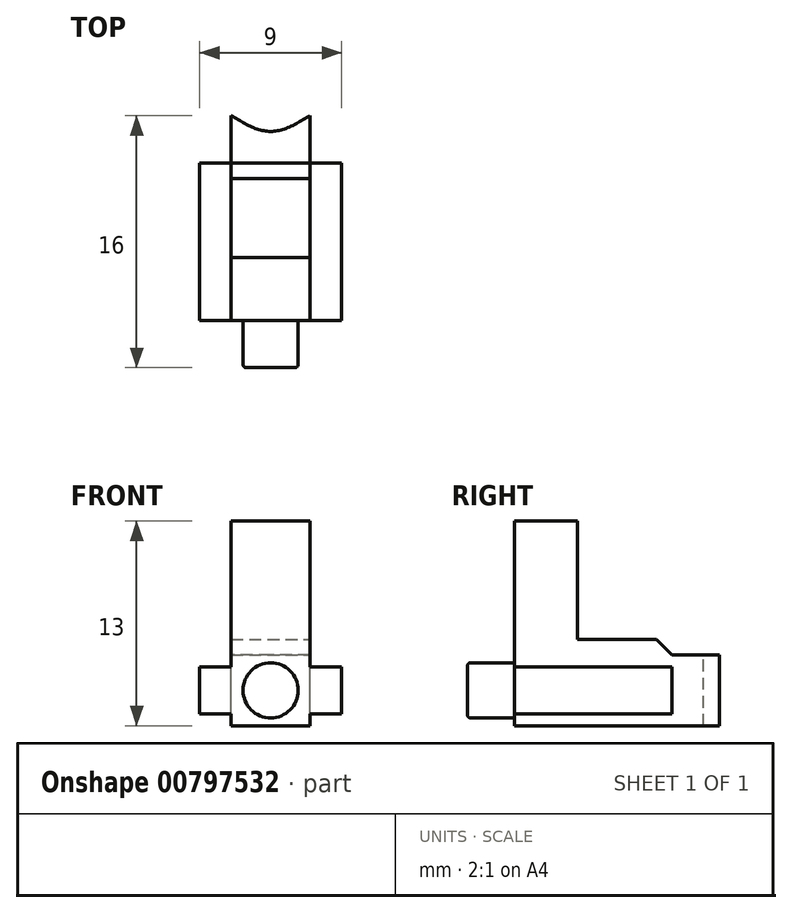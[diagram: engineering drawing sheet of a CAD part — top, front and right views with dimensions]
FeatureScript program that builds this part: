
annotation { "Feature Type Name" : "Feature", "Feature Type Description" : "" }
export const myFeature = defineFeature(function(context is Context, id is Id, definition is map)
    precondition{}
    {
        {
            var Q0;
            Q0=qCreatedBy(makeId("Front.planeOp"),FACE);
            var sketch = newSketch(context, id + "F0", { "sketchPlane" : qUnion([Q0])});
            skLineSegment(sketch, "E0.bottom", {"start": v(0, 0) * mm, "end": v(5, 0) * mm});
            skLineSegment(sketch, "E0.top", {"start": v(0, 13) * mm, "end": v(5, 13) * mm});
            skLineSegment(sketch, "E0.left", {"start": v(0, 0) * mm, "end": v(0, 13) * mm});
            skLineSegment(sketch, "E0.right", {"start": v(5, 0) * mm, "end": v(5, 13) * mm});
            skLineSegment(sketch, "E1", {"start": v(0, 4.5) * mm, "end": v(5, 4.5) * mm});
            skPoint(sketch, "E2", {"position": v(2.5, 2.25) * mm});
            skCircle(sketch, "E3", {"center": v(2.5, 2.25) * mm, "radius": 1.75 * mm});
            skLineSegment(sketch, "E4", {"start": v(5, 3.75) * mm, "end": v(7, 3.75) * mm});
            skLineSegment(sketch, "E5", {"start": v(7, 3.75) * mm, "end": v(7, 0.75) * mm});
            skLineSegment(sketch, "E6", {"start": v(7, 0.75) * mm, "end": v(5, 0.75) * mm});
            skLineSegment(sketch, "E7", {"start": v(0, 0.75) * mm, "end": v(-2, 0.75) * mm});
            skLineSegment(sketch, "E8", {"start": v(-2, 0.75) * mm, "end": v(-2, 3.75) * mm});
            skLineSegment(sketch, "E9", {"start": v(-2, 3.75) * mm, "end": v(0, 3.75) * mm});
            skLineSegment(sketch, "E10", {"start": v(0, 5.5) * mm, "end": v(5, 5.5) * mm});
            skSolve(sketch);
        }
        {
            var Q0;
            {var subQ0=sQuery(id+"F0.wireOp",EDGE,"E0.top");Q0=makeQuery(id+"F0.imprint","IMPRINT",FACE,{"disambiguationData":[TD([[makeQuery(id+"F0.imprint","IMPRINT",EDGE,{"derivedFrom":subQ0}),-1.0]])]});}
            var Q1;
            {var subQ4=sQuery(id+"F0.wireOp",EDGE,"E0.bottom");Q1=makeQuery(id+"F0.imprint","IMPRINT",FACE,{"disambiguationData":[TD([[makeQuery(id+"F0.imprint","IMPRINT",EDGE,{"derivedFrom":subQ4}),1.0]])]});}
            var Q2;
            Q2=makeQuery(id+"F0.imprint","IMPRINT",FACE,{"disambiguationData":[TD([[makeQuery(id+"F0.imprint","IMPRINT",EDGE,{"derivedFrom":sQuery(id+"F0.wireOp",EDGE,"E3")}),1.0]])]});
            var Q3;
            {var subQ0=sQuery(id+"F0.wireOp",EDGE,"E1");Q3=makeQuery(id+"F0.imprint","IMPRINT",FACE,{"disambiguationData":[TD([[makeQuery(id+"F0.imprint","IMPRINT",EDGE,{"derivedFrom":subQ0}),1.0]])]});}
            extrude(context, id + "F1", {"entities" : qUnion([Q0, Q1, Q2, Q3]), "oppositeDirection" : true, "depth" : 4 * mm, "offsetDistance" : 25 * mm});
        }
        {
            var Q0;
            Q0=makeQuery(id+"F0.imprint","IMPRINT",FACE,{"disambiguationData":[TD([[makeQuery(id+"F0.imprint","IMPRINT",EDGE,{"derivedFrom":sQuery(id+"F0.wireOp",EDGE,"E3")}),1.0]])]});
            extrude(context, id + "F2", {"entities" : qUnion([Q0]), "operationType" : NewBodyOperationType.ADD, "depth" : 3 * mm, "offsetDistance" : 25 * mm});
        }
        {
            var Q0;
            {var subQ0=sQuery(id+"F0.wireOp",EDGE,"E4");Q0=makeQuery(id+"F0.imprint","IMPRINT",FACE,{"disambiguationData":[TD([[makeQuery(id+"F0.imprint","IMPRINT",EDGE,{"derivedFrom":subQ0}),-1.0]])]});}
            var Q1;
            {var subQ0=sQuery(id+"F0.wireOp",EDGE,"E7");Q1=makeQuery(id+"F0.imprint","IMPRINT",FACE,{"disambiguationData":[TD([[makeQuery(id+"F0.imprint","IMPRINT",EDGE,{"derivedFrom":subQ0}),-1.0]])]});}
            var Q2;
            {var subQ0=sQuery(id+"F0.wireOp",EDGE,"E1");Q2=makeQuery(id+"F0.imprint","IMPRINT",FACE,{"disambiguationData":[TD([[makeQuery(id+"F0.imprint","IMPRINT",EDGE,{"derivedFrom":subQ0}),1.0]])]});}
            var Q3;
            {var subQ4=sQuery(id+"F0.wireOp",EDGE,"E0.bottom");Q3=makeQuery(id+"F0.imprint","IMPRINT",FACE,{"disambiguationData":[TD([[makeQuery(id+"F0.imprint","IMPRINT",EDGE,{"derivedFrom":subQ4}),1.0]])]});}
            var Q4;
            Q4=makeQuery(id+"F0.imprint","IMPRINT",FACE,{"disambiguationData":[TD([[makeQuery(id+"F0.imprint","IMPRINT",EDGE,{"derivedFrom":sQuery(id+"F0.wireOp",EDGE,"E3")}),1.0]])]});
            extrude(context, id + "F3", {"entities" : qUnion([Q0, Q1, Q2, Q3, Q4]), "operationType" : NewBodyOperationType.ADD, "oppositeDirection" : true, "depth" : 10 * mm, "offsetDistance" : 25 * mm});
        }
        {
            var Q0;
            Q0=makeQuery(id+"F0.imprint","IMPRINT",FACE,{"disambiguationData":[TD([[makeQuery(id+"F0.imprint","IMPRINT",EDGE,{"derivedFrom":sQuery(id+"F0.wireOp",EDGE,"E3")}),1.0]])]});
            var Q1;
            {var subQ4=sQuery(id+"F0.wireOp",EDGE,"E0.bottom");Q1=makeQuery(id+"F0.imprint","IMPRINT",FACE,{"disambiguationData":[TD([[makeQuery(id+"F0.imprint","IMPRINT",EDGE,{"derivedFrom":subQ4}),1.0]])]});}
            extrude(context, id + "F4", {"entities" : qUnion([Q0, Q1]), "operationType" : NewBodyOperationType.ADD, "oppositeDirection" : true, "depth" : 13 * mm, "offsetDistance" : 25 * mm});
        }
        {
            var Q0;
            Q0=makeQuery(id+"F3.opExtrude","CAP_EDGE",EDGE,{"disambiguationData":[OSD([sQuery(id+"F0.wireOp",EDGE,"E10")])],"isStart":false});
            chamfer(context, id + "F5", {"entities" : qUnion([Q0]), "width" : 1 * mm, "tangentPropagation" : true});
        }
        {
            var Q0;
            Q0=makeQuery(id+"F4.opExtrude","SWEPT_FACE",FACE,{"disambiguationData":[OSD([sQuery(id+"F0.wireOp",EDGE,"E1")])]});
            var sketch = newSketch(context, id + "F6", { "sketchPlane" : qUnion([Q0])});
            skLineSegment(sketch, "E11", {"start": v(2.5, 13) * mm, "end": v(2.5, 12) * mm});
            skFitSpline(sketch, "E12", {"points": [v(5, 13) * mm, v(2.5, 12) * mm, v(0, 13) * mm], "startDerivative": vector(-5, -3) * mm, "endDerivative": vector(-5, 3) * mm});
            skSolve(sketch);
        }
        {
            var Q0;
            {var subQ0=sQuery(id+"F6.wireOp",EDGE,"E11");Q0=makeQuery(id+"F6.imprint","IMPRINT",FACE,{"disambiguationData":[TD([[makeQuery(id+"F6.imprint","IMPRINT",EDGE,{"derivedFrom":subQ0}),1.0]])]});}
            var Q1;
            {var subQ0=sQuery(id+"F6.wireOp",EDGE,"E11");Q1=makeQuery(id+"F6.imprint","IMPRINT",FACE,{"disambiguationData":[TD([[makeQuery(id+"F6.imprint","IMPRINT",EDGE,{"derivedFrom":subQ0}),-1.0]])]});}
            extrude(context, id + "F7", {"entities" : qUnion([Q0, Q1]), "operationType" : NewBodyOperationType.REMOVE, "endBound" : BoundingType.THROUGH_ALL, "oppositeDirection" : true, "depth" : 25 * mm, "offsetDistance" : 25 * mm});
        }
        {
            var Q0;
            Q0=makeQuery(id+"F2.opExtrude","CAP_EDGE",EDGE,{"disambiguationData":[OSD([sQuery(id+"F0.wireOp",EDGE,"E3")])],"isStart":false});
            fillet(context, id + "F8", {"entities" : qUnion([Q0]), "radius" : 0.2 * mm, "tangentPropagation" : true, "allowEdgeOverflow" : false});
        }
    });
